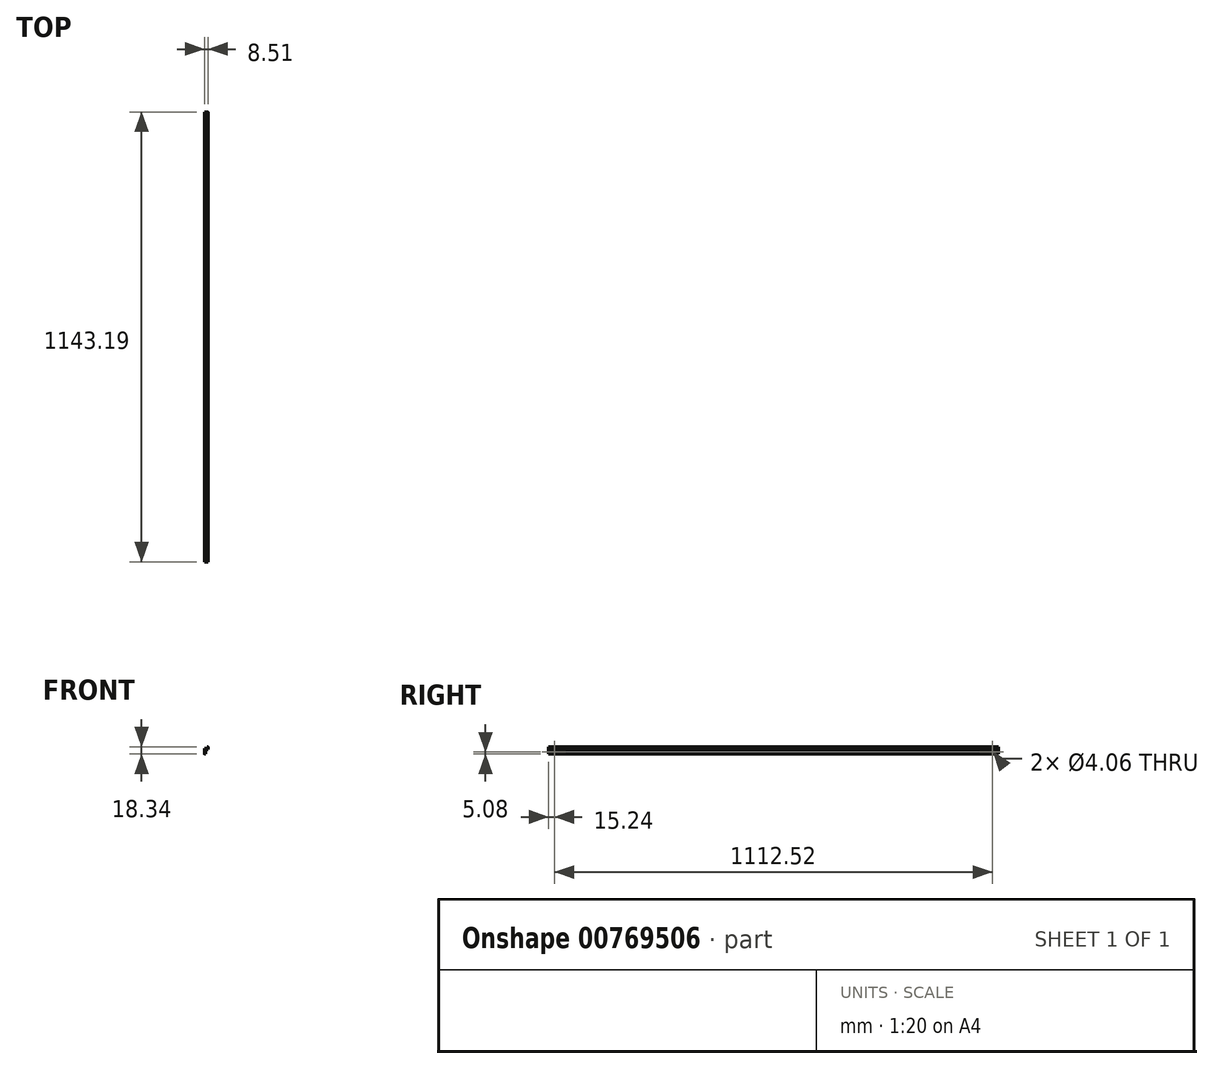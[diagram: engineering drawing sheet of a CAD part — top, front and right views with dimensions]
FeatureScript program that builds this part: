
annotation { "Feature Type Name" : "Feature", "Feature Type Description" : "" }
export const myFeature = defineFeature(function(context is Context, id is Id, definition is map)
    precondition{}
    {
        {
            var Q0;
            Q0=qCreatedBy(makeId("Front.planeOp"),FACE);
            var sketch = newSketch(context, id + "F0", { "sketchPlane" : qUnion([Q0])});
            skLineSegment(sketch, "E0.bottom", {"start": v(0, 0) * mm, "end": v(8.5, 0) * mm});
            skLineSegment(sketch, "E0.top", {"start": v(0, 18.34) * mm, "end": v(8.5, 18.34) * mm});
            skLineSegment(sketch, "E0.left", {"start": v(0, 0) * mm, "end": v(0, 18.34) * mm});
            skLineSegment(sketch, "E0.right", {"start": v(8.5, 0) * mm, "end": v(8.5, 18.34) * mm});
            skSolve(sketch);
        }
        {
            var Q0;
            Q0=qSketchRegion(id+"F0",true);
            extrude(context, id + "F1", {"entities" : qUnion([Q0]), "depth" : 1143 * mm, "offsetDistance" : 25.4 * mm});
        }
        {
            var Q0;
            Q0=makeQuery(id+"F1.opExtrude","CAP_FACE",FACE,{"disambiguationData":[OSD([sQuery(id+"F0.wireOp",EDGE,"E0.bottom"),sQuery(id+"F0.wireOp",EDGE,"E0.top"),sQuery(id+"F0.wireOp",EDGE,"E0.left"),sQuery(id+"F0.wireOp",EDGE,"E0.right")])],"isStart":false});
            var sketch = newSketch(context, id + "F2", { "sketchPlane" : qUnion([Q0])});
            skLineSegment(sketch, "E1.bottom", {"start": v(0, 18.34) * mm, "end": v(6.35, 18.34) * mm});
            skLineSegment(sketch, "E1.top", {"start": v(0, 13.59) * mm, "end": v(6.35, 13.59) * mm});
            skLineSegment(sketch, "E1.left", {"start": v(0, 18.34) * mm, "end": v(0, 13.59) * mm});
            skLineSegment(sketch, "E1.right", {"start": v(6.35, 18.34) * mm, "end": v(6.35, 13.59) * mm});
            skPoint(sketch, "E2.oppositeSnap0", {"position": v(2.16, 0) * mm});
            skLineSegment(sketch, "E2.bottom", {"start": v(8.5, 0) * mm, "end": v(2.16, 0) * mm});
            skLineSegment(sketch, "E2.top", {"start": v(8.5, 11.43) * mm, "end": v(2.16, 11.43) * mm});
            skLineSegment(sketch, "E2.left", {"start": v(8.5, 0) * mm, "end": v(8.5, 11.43) * mm});
            skLineSegment(sketch, "E2.right", {"start": v(2.16, 0) * mm, "end": v(2.16, 11.43) * mm});
            skSolve(sketch);
        }
        {
            var Q0;
            Q0=qSketchRegion(id+"F2",true);
            extrude(context, id + "F3", {"entities" : qUnion([Q0]), "operationType" : NewBodyOperationType.REMOVE, "endBound" : BoundingType.THROUGH_ALL, "oppositeDirection" : true, "depth" : 25.4 * mm, "offsetDistance" : 25.4 * mm});
        }
        {
            var Q0;
            Q0=makeQuery(id+"F3.boolean.opBoolean","COPY",EDGE,{"derivedFrom":makeQuery(id+"F3.opExtrude","SWEPT_EDGE",EDGE,{"disambiguationData":[OSD([sQuery(id+"F0.wireOp",EDGE,"E0.top"),sQuery(id+"F2.wireOp",EDGE,"E1.bottom"),sQuery(id+"F2.wireOp",EDGE,"E1.right")])]})});
            var Q1;
            Q1=makeQuery(id+"F1.opExtrude","SWEPT_EDGE",EDGE,{"disambiguationData":[OSD([sQuery(id+"F0.wireOp",EDGE,"E0.top"),sQuery(id+"F0.wireOp",EDGE,"E0.right")])]});
            var Q2;
            Q2=makeQuery(id+"F3.boolean.opBoolean","COPY",EDGE,{"derivedFrom":makeQuery(id+"F3.opExtrude","SWEPT_EDGE",EDGE,{"disambiguationData":[OSD([sQuery(id+"F0.wireOp",EDGE,"E0.bottom"),sQuery(id+"F2.wireOp",EDGE,"E2.bottom"),sQuery(id+"F2.wireOp",EDGE,"E2.right")])]})});
            var Q3;
            Q3=makeQuery(id+"F1.opExtrude","SWEPT_EDGE",EDGE,{"disambiguationData":[OSD([sQuery(id+"F0.wireOp",EDGE,"E0.bottom"),sQuery(id+"F0.wireOp",EDGE,"E0.left")])]});
            var Q4;
            Q4=makeQuery(id+"F3.boolean.opBoolean","COPY",EDGE,{"derivedFrom":makeQuery(id+"F3.opExtrude","SWEPT_EDGE",EDGE,{"disambiguationData":[OSD([sQuery(id+"F0.wireOp",EDGE,"E0.left"),sQuery(id+"F2.wireOp",EDGE,"E1.top"),sQuery(id+"F2.wireOp",EDGE,"E1.left")])]})});
            fillet(context, id + "F4", {"entities" : qUnion([Q0, Q1, Q2, Q3, Q4]), "radius" : 0.13 * mm, "tangentPropagation" : true, "allowEdgeOverflow" : false});
        }
        {
            var Q0;
            Q0=makeQuery(id+"F1.opExtrude","CAP_FACE",FACE,{"disambiguationData":[OSD([sQuery(id+"F0.wireOp",EDGE,"E0.bottom"),sQuery(id+"F0.wireOp",EDGE,"E0.top"),sQuery(id+"F0.wireOp",EDGE,"E0.left"),sQuery(id+"F0.wireOp",EDGE,"E0.right")])],"isStart":false});
            var sketch = newSketch(context, id + "F5", { "sketchPlane" : qUnion([Q0])});
            skLineSegment(sketch, "E3", {"start": v(3.68, 11.43) * mm, "end": v(2.16, 10.16) * mm});
            skLineSegment(sketch, "E4", {"start": v(2.16, 10.16) * mm, "end": v(2.16, 11.43) * mm});
            skLineSegment(sketch, "E5", {"start": v(2.16, 11.43) * mm, "end": v(3.68, 11.43) * mm});
            skSolve(sketch);
        }
        {
            var Q0;
            Q0=makeQuery(id+"F5.imprint","IMPRINT",FACE,{"disambiguationData":[TD([[makeQuery(id+"F5.imprint","IMPRINT",EDGE,{"derivedFrom":sQuery(id+"F5.wireOp",EDGE,"E3")}),-1.0]])]});
            extrude(context, id + "F6", {"entities" : qUnion([Q0]), "endBound" : BoundingType.THROUGH_ALL, "oppositeDirection" : true, "depth" : 25.4 * mm, "offsetDistance" : 25.4 * mm});
        }
        {
            var Q0;
            Q0=makeQuery(id+"F3.boolean.opBoolean","COPY",FACE,{"derivedFrom":makeQuery(id+"F3.opExtrude","SWEPT_FACE",FACE,{"disambiguationData":[OSD([sQuery(id+"F2.wireOp",EDGE,"E2.right")])]})});
            var sketch = newSketch(context, id + "F7", { "sketchPlane" : qUnion([Q0])});
            skCircle(sketch, "E6", {"center": v(-1127.76, 5.08) * mm, "radius": 2.03 * mm});
            skCircle(sketch, "E7", {"center": v(-15.24, 5.08) * mm, "radius": 2.03 * mm});
            skSolve(sketch);
        }
        {
            var Q0;
            Q0=qSketchRegion(id+"F7",true);
            extrude(context, id + "F8", {"entities" : qUnion([Q0]), "operationType" : NewBodyOperationType.REMOVE, "endBound" : BoundingType.UP_TO_NEXT, "oppositeDirection" : true, "depth" : 25.4 * mm, "offsetDistance" : 25.4 * mm});
        }
    });
